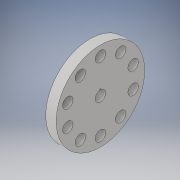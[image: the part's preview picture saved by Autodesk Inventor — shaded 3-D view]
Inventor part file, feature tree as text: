
AUTODESK INVENTOR PART (.ipt)
format: ipt  version: 2017 (Build 210142000, 142)  size: 151,552 bytes
history: native  units: in
note: dims shown in document units (in); Inventor stores cm internally (conversion verified against a paired STEP export)
features: sketch x4, hole x2, revolve x1, extrude x1
ambient origin geometry x8: Origin, YZ Plane, XZ Plane, XY Plane, X Axis, Y Axis, Z Axis, Center Point
bodies: Solid1 (feature_tree)
feature tree (8):
  revolve  "Revolution1"  [1 undecoded]
  hole  "Hole1"  [1 undecoded]
  hole  "Hole2"  [1 undecoded]
  extrude  "Extrusion1"  Depth=1.0in TaperAngle=360.0deg
  sketch  "Sketch1"  dims[d0=0.625in d1=0.5in]
  sketch  "Sketch2"  dims[d2=1.5in d3=0.5in]
  sketch  "Sketch3"  dims[d4=90.0deg]
  sketch  "Sketch4"  dims[d5=0.5in d6=0.75in d7=0.375in d8=0.25in d9=0.5635in d10=1.0in d11=0.8108in d13=3.3in d14=3.937in d16=360.0deg d18=0.5in d19=0.75in d20=0.375in d21=0.25in d22=0.5635in d23=1.0in d24=0.8108in d27=0.025in d28=0.05in d29=0.05in d30=0.0in d31=0.0in]
note: 3 required parameter values undecoded (feature->parameter linkage not recoverable at this tier; creation-order binding heuristic only, values carry confidence <= 0.55)